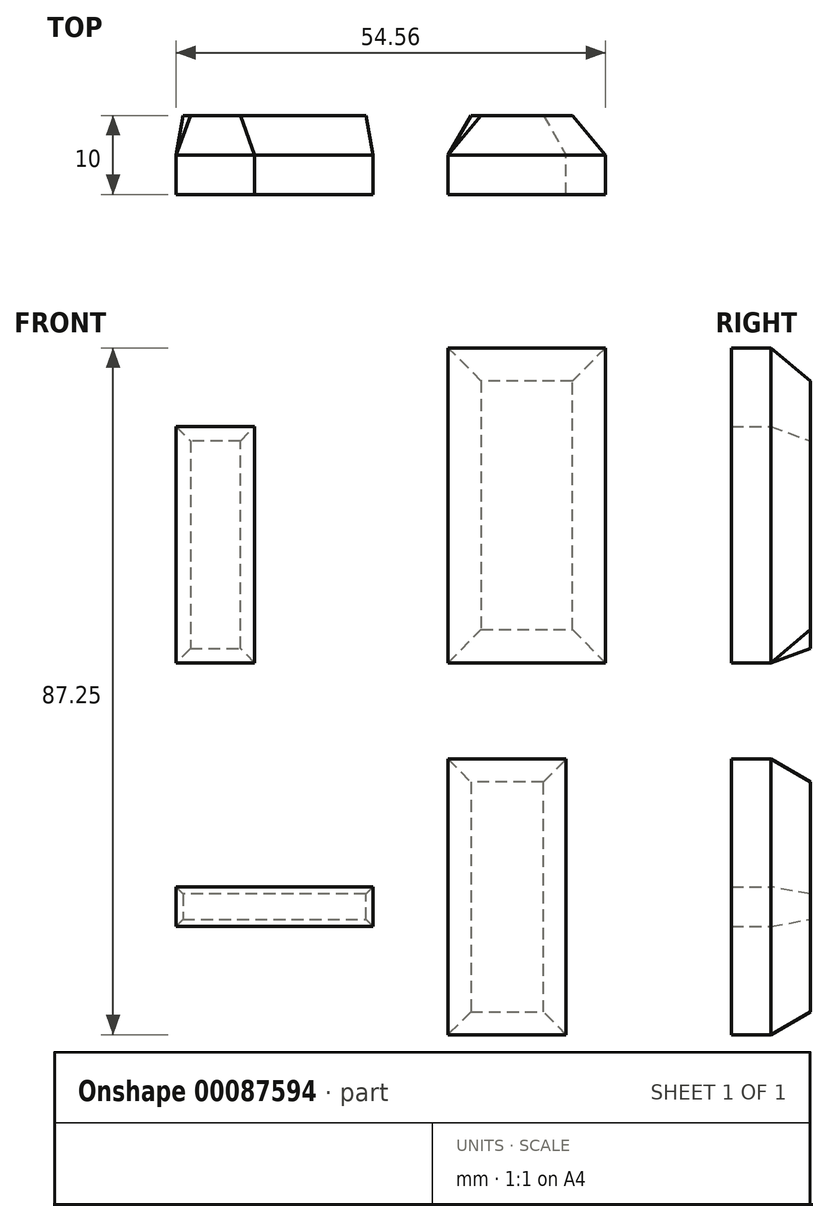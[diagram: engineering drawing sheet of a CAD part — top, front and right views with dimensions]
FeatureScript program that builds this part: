
annotation { "Feature Type Name" : "Feature", "Feature Type Description" : "" }
export const myFeature = defineFeature(function(context is Context, id is Id, definition is map)
    precondition{}
    {
        {
            var Q0;
            Q0=qCreatedBy(makeId("Front.planeOp"),FACE);
            var sketch = newSketch(context, id + "F0", { "sketchPlane" : qUnion([Q0])});
            skLineSegment(sketch, "E0.bottom", {"start": v(0, 0) * mm, "end": v(20, 0) * mm});
            skLineSegment(sketch, "E0.top", {"start": v(0, 40) * mm, "end": v(20, 40) * mm});
            skLineSegment(sketch, "E0.left", {"start": v(0, 0) * mm, "end": v(0, 40) * mm});
            skLineSegment(sketch, "E0.right", {"start": v(20, 0) * mm, "end": v(20, 40) * mm});
            skLineSegment(sketch, "E1.bottom", {"start": v(-24.56, 0) * mm, "end": v(-34.56, 0) * mm});
            skLineSegment(sketch, "E1.top", {"start": v(-24.56, 30) * mm, "end": v(-34.56, 30) * mm});
            skLineSegment(sketch, "E1.left", {"start": v(-24.56, 0) * mm, "end": v(-24.56, 30) * mm});
            skLineSegment(sketch, "E1.right", {"start": v(-34.56, 0) * mm, "end": v(-34.56, 30) * mm});
            skLineSegment(sketch, "E2.bottom", {"start": v(-34.56, -28.49) * mm, "end": v(-9.56, -28.49) * mm});
            skLineSegment(sketch, "E2.top", {"start": v(-34.56, -33.49) * mm, "end": v(-9.56, -33.49) * mm});
            skLineSegment(sketch, "E2.left", {"start": v(-34.56, -28.49) * mm, "end": v(-34.56, -33.49) * mm});
            skLineSegment(sketch, "E2.right", {"start": v(-9.56, -28.49) * mm, "end": v(-9.56, -33.49) * mm});
            skLineSegment(sketch, "E3.bottom", {"start": v(0, -12.25) * mm, "end": v(15, -12.25) * mm});
            skLineSegment(sketch, "E3.top", {"start": v(0, -47.25) * mm, "end": v(15, -47.25) * mm});
            skLineSegment(sketch, "E3.left", {"start": v(0, -12.25) * mm, "end": v(0, -47.25) * mm});
            skLineSegment(sketch, "E3.right", {"start": v(15, -12.25) * mm, "end": v(15, -47.25) * mm});
            skSolve(sketch);
        }
        {
            var Q0;
            Q0 = qSketchRegion(id + "F0", true);
            extrude(context, id + "F1", {"entities" : qUnion([Q0]), "depth" : 5 * mm});
        }
        {
            var Q0;
            Q0=makeQuery(id+"F1.opExtrude","CAP_FACE",FACE,{"disambiguationData":[OSD([sQuery(id+"F0.wireOp",EDGE,"E0.bottom"),sQuery(id+"F0.wireOp",EDGE,"E0.top"),sQuery(id+"F0.wireOp",EDGE,"E0.left"),sQuery(id+"F0.wireOp",EDGE,"E0.right")])],"isStart":true});
            extrude(context, id + "F2", {"entities" : qUnion([Q0]), "operationType" : NewBodyOperationType.ADD, "depth" : 5 * mm, "hasDraft" : true, "draftAngle" : 40 * degree, "draftPullDirection" : true});
        }
        {
            var Q0;
            Q0=makeQuery(id+"F1.opExtrude","CAP_FACE",FACE,{"disambiguationData":[OSD([sQuery(id+"F0.wireOp",EDGE,"E3.bottom"),sQuery(id+"F0.wireOp",EDGE,"E3.top"),sQuery(id+"F0.wireOp",EDGE,"E3.left"),sQuery(id+"F0.wireOp",EDGE,"E3.right")])],"isStart":true});
            extrude(context, id + "F3", {"entities" : qUnion([Q0]), "operationType" : NewBodyOperationType.ADD, "depth" : 5 * mm, "hasDraft" : true, "draftAngle" : 30 * degree, "draftPullDirection" : true});
        }
        {
            var Q0;
            Q0=makeQuery(id+"F1.opExtrude","CAP_FACE",FACE,{"disambiguationData":[OSD([sQuery(id+"F0.wireOp",EDGE,"E1.bottom"),sQuery(id+"F0.wireOp",EDGE,"E1.top"),sQuery(id+"F0.wireOp",EDGE,"E1.left"),sQuery(id+"F0.wireOp",EDGE,"E1.right")])],"isStart":true});
            extrude(context, id + "F4", {"entities" : qUnion([Q0]), "operationType" : NewBodyOperationType.ADD, "depth" : 5 * mm, "hasDraft" : true, "draftAngle" : 20 * degree, "draftPullDirection" : true});
        }
        {
            var Q0;
            Q0=makeQuery(id+"F1.opExtrude","CAP_FACE",FACE,{"disambiguationData":[OSD([sQuery(id+"F0.wireOp",EDGE,"E2.bottom"),sQuery(id+"F0.wireOp",EDGE,"E2.top"),sQuery(id+"F0.wireOp",EDGE,"E2.left"),sQuery(id+"F0.wireOp",EDGE,"E2.right")])],"isStart":true});
            extrude(context, id + "F5", {"entities" : qUnion([Q0]), "operationType" : NewBodyOperationType.ADD, "depth" : 5 * mm, "hasDraft" : true, "draftAngle" : 10 * degree, "draftPullDirection" : true});
        }
    });
